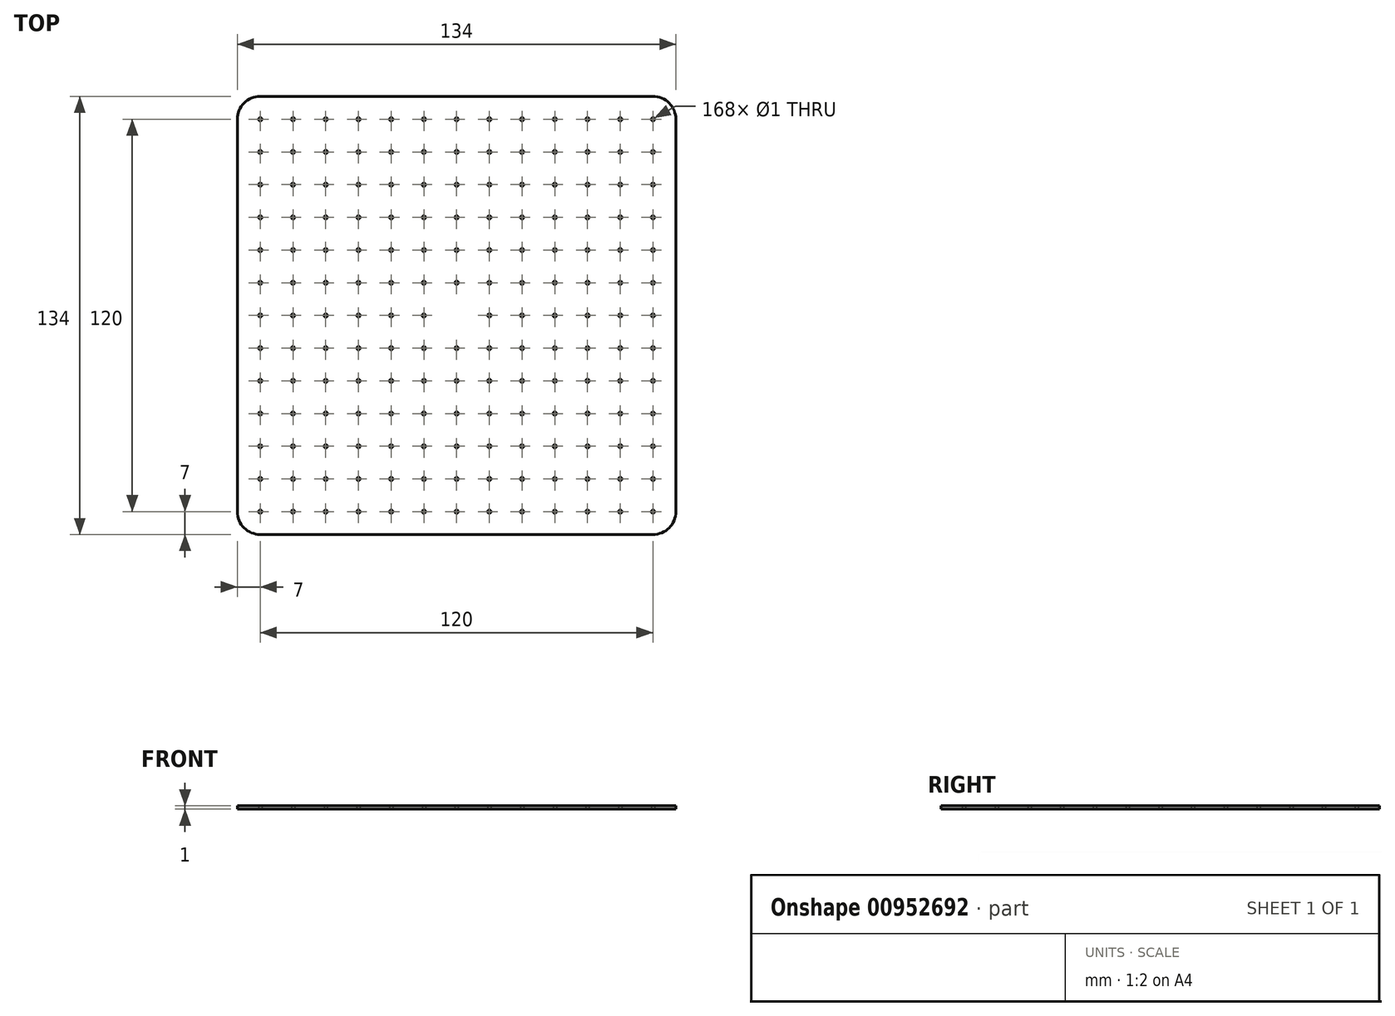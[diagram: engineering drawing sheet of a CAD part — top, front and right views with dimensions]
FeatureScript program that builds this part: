
annotation { "Feature Type Name" : "Feature", "Feature Type Description" : "" }
export const myFeature = defineFeature(function(context is Context, id is Id, definition is map)
    precondition{}
    {
        {
            var Q0;
            Q0=qCreatedBy(makeId("Top.planeOp"),FACE);
            var sketch = newSketch(context, id + "F0", { "sketchPlane" : qUnion([Q0])});
            skLineSegment(sketch, "E0.bottom", {"start": v(-60, -67) * mm, "end": v(60, -67) * mm});
            skLineSegment(sketch, "E0.top", {"start": v(-60, 67) * mm, "end": v(60, 67) * mm});
            skLineSegment(sketch, "E0.left", {"start": v(-67, -60) * mm, "end": v(-67, 60) * mm});
            skLineSegment(sketch, "E0.right", {"start": v(67, -60) * mm, "end": v(67, 60) * mm});
            skPoint(sketch, "E0.middle", {"position": v(0, 0) * mm});
            skPoint(sketch, "E1.visualSharp", {"position": v(-67, -67) * mm});
            skArc(sketch, "E1.filletArc", {"start": v(-67, -60) * mm, "mid": v(-64.95, -64.95) * mm, "end": v(-60, -67) * mm});
            skPoint(sketch, "E2.visualSharp", {"position": v(-67, 67) * mm});
            skArc(sketch, "E2.filletArc", {"start": v(-60, 67) * mm, "mid": v(-64.95, 64.95) * mm, "end": v(-67, 60) * mm});
            skPoint(sketch, "E3.visualSharp", {"position": v(67, 67) * mm});
            skArc(sketch, "E3.filletArc", {"start": v(67, 60) * mm, "mid": v(64.95, 64.95) * mm, "end": v(60, 67) * mm});
            skPoint(sketch, "E4.visualSharp", {"position": v(67, -67) * mm});
            skArc(sketch, "E4.filletArc", {"start": v(60, -67) * mm, "mid": v(64.95, -64.95) * mm, "end": v(67, -60) * mm});
            skCircle(sketch, "E5", {"center": v(-60, 60) * mm, "radius": 0.5 * mm});
            skCircle(sketch, "E6.0.1.0", {"center": v(-60, 50) * mm, "radius": 0.5 * mm});
            skCircle(sketch, "E6.0.2.0", {"center": v(-60, 40) * mm, "radius": 0.5 * mm});
            skCircle(sketch, "E6.0.3.0", {"center": v(-60, 30) * mm, "radius": 0.5 * mm});
            skCircle(sketch, "E6.0.4.0", {"center": v(-60, 20) * mm, "radius": 0.5 * mm});
            skCircle(sketch, "E6.0.5.0", {"center": v(-60, 10) * mm, "radius": 0.5 * mm});
            skCircle(sketch, "E6.0.6.0", {"center": v(-60, 0) * mm, "radius": 0.5 * mm});
            skCircle(sketch, "E6.0.7.0", {"center": v(-60, -10) * mm, "radius": 0.5 * mm});
            skCircle(sketch, "E6.0.8.0", {"center": v(-60, -20) * mm, "radius": 0.5 * mm});
            skCircle(sketch, "E6.0.9.0", {"center": v(-60, -30) * mm, "radius": 0.5 * mm});
            skCircle(sketch, "E6.0.10.0", {"center": v(-60, -40) * mm, "radius": 0.5 * mm});
            skCircle(sketch, "E6.0.11.0", {"center": v(-60, -50) * mm, "radius": 0.5 * mm});
            skCircle(sketch, "E6.1.0.0", {"center": v(-50, 60) * mm, "radius": 0.5 * mm});
            skCircle(sketch, "E6.1.1.0", {"center": v(-50, 50) * mm, "radius": 0.5 * mm});
            skCircle(sketch, "E6.1.2.0", {"center": v(-50, 40) * mm, "radius": 0.5 * mm});
            skCircle(sketch, "E6.1.3.0", {"center": v(-50, 30) * mm, "radius": 0.5 * mm});
            skCircle(sketch, "E6.1.4.0", {"center": v(-50, 20) * mm, "radius": 0.5 * mm});
            skCircle(sketch, "E6.1.5.0", {"center": v(-50, 10) * mm, "radius": 0.5 * mm});
            skCircle(sketch, "E6.1.6.0", {"center": v(-50, 0) * mm, "radius": 0.5 * mm});
            skCircle(sketch, "E6.1.7.0", {"center": v(-50, -10) * mm, "radius": 0.5 * mm});
            skCircle(sketch, "E6.1.8.0", {"center": v(-50, -20) * mm, "radius": 0.5 * mm});
            skCircle(sketch, "E6.1.9.0", {"center": v(-50, -30) * mm, "radius": 0.5 * mm});
            skCircle(sketch, "E6.1.10.0", {"center": v(-50, -40) * mm, "radius": 0.5 * mm});
            skCircle(sketch, "E6.1.11.0", {"center": v(-50, -50) * mm, "radius": 0.5 * mm});
            skCircle(sketch, "E6.2.0.0", {"center": v(-40, 60) * mm, "radius": 0.5 * mm});
            skCircle(sketch, "E6.2.1.0", {"center": v(-40, 50) * mm, "radius": 0.5 * mm});
            skCircle(sketch, "E6.2.2.0", {"center": v(-40, 40) * mm, "radius": 0.5 * mm});
            skCircle(sketch, "E6.2.3.0", {"center": v(-40, 30) * mm, "radius": 0.5 * mm});
            skCircle(sketch, "E6.2.4.0", {"center": v(-40, 20) * mm, "radius": 0.5 * mm});
            skCircle(sketch, "E6.2.5.0", {"center": v(-40, 10) * mm, "radius": 0.5 * mm});
            skCircle(sketch, "E6.2.6.0", {"center": v(-40, 0) * mm, "radius": 0.5 * mm});
            skCircle(sketch, "E6.2.7.0", {"center": v(-40, -10) * mm, "radius": 0.5 * mm});
            skCircle(sketch, "E6.2.8.0", {"center": v(-40, -20) * mm, "radius": 0.5 * mm});
            skCircle(sketch, "E6.2.9.0", {"center": v(-40, -30) * mm, "radius": 0.5 * mm});
            skCircle(sketch, "E6.2.10.0", {"center": v(-40, -40) * mm, "radius": 0.5 * mm});
            skCircle(sketch, "E6.2.11.0", {"center": v(-40, -50) * mm, "radius": 0.5 * mm});
            skCircle(sketch, "E6.3.0.0", {"center": v(-30, 60) * mm, "radius": 0.5 * mm});
            skCircle(sketch, "E6.3.1.0", {"center": v(-30, 50) * mm, "radius": 0.5 * mm});
            skCircle(sketch, "E6.3.2.0", {"center": v(-30, 40) * mm, "radius": 0.5 * mm});
            skCircle(sketch, "E6.3.3.0", {"center": v(-30, 30) * mm, "radius": 0.5 * mm});
            skCircle(sketch, "E6.3.4.0", {"center": v(-30, 20) * mm, "radius": 0.5 * mm});
            skCircle(sketch, "E6.3.5.0", {"center": v(-30, 10) * mm, "radius": 0.5 * mm});
            skCircle(sketch, "E6.3.6.0", {"center": v(-30, 0) * mm, "radius": 0.5 * mm});
            skCircle(sketch, "E6.3.7.0", {"center": v(-30, -10) * mm, "radius": 0.5 * mm});
            skCircle(sketch, "E6.3.8.0", {"center": v(-30, -20) * mm, "radius": 0.5 * mm});
            skCircle(sketch, "E6.3.9.0", {"center": v(-30, -30) * mm, "radius": 0.5 * mm});
            skCircle(sketch, "E6.3.10.0", {"center": v(-30, -40) * mm, "radius": 0.5 * mm});
            skCircle(sketch, "E6.3.11.0", {"center": v(-30, -50) * mm, "radius": 0.5 * mm});
            skCircle(sketch, "E6.4.0.0", {"center": v(-20, 60) * mm, "radius": 0.5 * mm});
            skCircle(sketch, "E6.4.1.0", {"center": v(-20, 50) * mm, "radius": 0.5 * mm});
            skCircle(sketch, "E6.4.2.0", {"center": v(-20, 40) * mm, "radius": 0.5 * mm});
            skCircle(sketch, "E6.4.3.0", {"center": v(-20, 30) * mm, "radius": 0.5 * mm});
            skCircle(sketch, "E6.4.4.0", {"center": v(-20, 20) * mm, "radius": 0.5 * mm});
            skCircle(sketch, "E6.4.5.0", {"center": v(-20, 10) * mm, "radius": 0.5 * mm});
            skCircle(sketch, "E6.4.6.0", {"center": v(-20, 0) * mm, "radius": 0.5 * mm});
            skCircle(sketch, "E6.4.7.0", {"center": v(-20, -10) * mm, "radius": 0.5 * mm});
            skCircle(sketch, "E6.4.8.0", {"center": v(-20, -20) * mm, "radius": 0.5 * mm});
            skCircle(sketch, "E6.4.9.0", {"center": v(-20, -30) * mm, "radius": 0.5 * mm});
            skCircle(sketch, "E6.4.10.0", {"center": v(-20, -40) * mm, "radius": 0.5 * mm});
            skCircle(sketch, "E6.4.11.0", {"center": v(-20, -50) * mm, "radius": 0.5 * mm});
            skCircle(sketch, "E6.5.0.0", {"center": v(-10, 60) * mm, "radius": 0.5 * mm});
            skCircle(sketch, "E6.5.1.0", {"center": v(-10, 50) * mm, "radius": 0.5 * mm});
            skCircle(sketch, "E6.5.2.0", {"center": v(-10, 40) * mm, "radius": 0.5 * mm});
            skCircle(sketch, "E6.5.3.0", {"center": v(-10, 30) * mm, "radius": 0.5 * mm});
            skCircle(sketch, "E6.5.4.0", {"center": v(-10, 20) * mm, "radius": 0.5 * mm});
            skCircle(sketch, "E6.5.5.0", {"center": v(-10, 10) * mm, "radius": 0.5 * mm});
            skCircle(sketch, "E6.5.6.0", {"center": v(-10, 0) * mm, "radius": 0.5 * mm});
            skCircle(sketch, "E6.5.7.0", {"center": v(-10, -10) * mm, "radius": 0.5 * mm});
            skCircle(sketch, "E6.5.8.0", {"center": v(-10, -20) * mm, "radius": 0.5 * mm});
            skCircle(sketch, "E6.5.9.0", {"center": v(-10, -30) * mm, "radius": 0.5 * mm});
            skCircle(sketch, "E6.5.10.0", {"center": v(-10, -40) * mm, "radius": 0.5 * mm});
            skCircle(sketch, "E6.5.11.0", {"center": v(-10, -50) * mm, "radius": 0.5 * mm});
            skCircle(sketch, "E6.6.0.0", {"center": v(0, 60) * mm, "radius": 0.5 * mm});
            skCircle(sketch, "E6.6.1.0", {"center": v(0, 50) * mm, "radius": 0.5 * mm});
            skCircle(sketch, "E6.6.2.0", {"center": v(0, 40) * mm, "radius": 0.5 * mm});
            skCircle(sketch, "E6.6.3.0", {"center": v(0, 30) * mm, "radius": 0.5 * mm});
            skCircle(sketch, "E6.6.4.0", {"center": v(0, 20) * mm, "radius": 0.5 * mm});
            skCircle(sketch, "E6.6.5.0", {"center": v(0, 10) * mm, "radius": 0.5 * mm});
            skCircle(sketch, "E6.6.6.0", {"center": v(0, 0) * mm, "radius": 0.5 * mm});
            skCircle(sketch, "E6.6.7.0", {"center": v(0, -10) * mm, "radius": 0.5 * mm});
            skCircle(sketch, "E6.6.8.0", {"center": v(0, -20) * mm, "radius": 0.5 * mm});
            skCircle(sketch, "E6.6.9.0", {"center": v(0, -30) * mm, "radius": 0.5 * mm});
            skCircle(sketch, "E6.6.10.0", {"center": v(0, -40) * mm, "radius": 0.5 * mm});
            skCircle(sketch, "E6.6.11.0", {"center": v(0, -50) * mm, "radius": 0.5 * mm});
            skCircle(sketch, "E6.7.0.0", {"center": v(10, 60) * mm, "radius": 0.5 * mm});
            skCircle(sketch, "E6.7.1.0", {"center": v(10, 50) * mm, "radius": 0.5 * mm});
            skCircle(sketch, "E6.7.2.0", {"center": v(10, 40) * mm, "radius": 0.5 * mm});
            skCircle(sketch, "E6.7.3.0", {"center": v(10, 30) * mm, "radius": 0.5 * mm});
            skCircle(sketch, "E6.7.4.0", {"center": v(10, 20) * mm, "radius": 0.5 * mm});
            skCircle(sketch, "E6.7.5.0", {"center": v(10, 10) * mm, "radius": 0.5 * mm});
            skCircle(sketch, "E6.7.6.0", {"center": v(10, 0) * mm, "radius": 0.5 * mm});
            skCircle(sketch, "E6.7.7.0", {"center": v(10, -10) * mm, "radius": 0.5 * mm});
            skCircle(sketch, "E6.7.8.0", {"center": v(10, -20) * mm, "radius": 0.5 * mm});
            skCircle(sketch, "E6.7.9.0", {"center": v(10, -30) * mm, "radius": 0.5 * mm});
            skCircle(sketch, "E6.7.10.0", {"center": v(10, -40) * mm, "radius": 0.5 * mm});
            skCircle(sketch, "E6.7.11.0", {"center": v(10, -50) * mm, "radius": 0.5 * mm});
            skCircle(sketch, "E6.8.0.0", {"center": v(20, 60) * mm, "radius": 0.5 * mm});
            skCircle(sketch, "E6.8.1.0", {"center": v(20, 50) * mm, "radius": 0.5 * mm});
            skCircle(sketch, "E6.8.2.0", {"center": v(20, 40) * mm, "radius": 0.5 * mm});
            skCircle(sketch, "E6.8.3.0", {"center": v(20, 30) * mm, "radius": 0.5 * mm});
            skCircle(sketch, "E6.8.4.0", {"center": v(20, 20) * mm, "radius": 0.5 * mm});
            skCircle(sketch, "E6.8.5.0", {"center": v(20, 10) * mm, "radius": 0.5 * mm});
            skCircle(sketch, "E6.8.6.0", {"center": v(20, 0) * mm, "radius": 0.5 * mm});
            skCircle(sketch, "E6.8.7.0", {"center": v(20, -10) * mm, "radius": 0.5 * mm});
            skCircle(sketch, "E6.8.8.0", {"center": v(20, -20) * mm, "radius": 0.5 * mm});
            skCircle(sketch, "E6.8.9.0", {"center": v(20, -30) * mm, "radius": 0.5 * mm});
            skCircle(sketch, "E6.8.10.0", {"center": v(20, -40) * mm, "radius": 0.5 * mm});
            skCircle(sketch, "E6.8.11.0", {"center": v(20, -50) * mm, "radius": 0.5 * mm});
            skCircle(sketch, "E6.9.0.0", {"center": v(30, 60) * mm, "radius": 0.5 * mm});
            skCircle(sketch, "E6.9.1.0", {"center": v(30, 50) * mm, "radius": 0.5 * mm});
            skCircle(sketch, "E6.9.2.0", {"center": v(30, 40) * mm, "radius": 0.5 * mm});
            skCircle(sketch, "E6.9.3.0", {"center": v(30, 30) * mm, "radius": 0.5 * mm});
            skCircle(sketch, "E6.9.4.0", {"center": v(30, 20) * mm, "radius": 0.5 * mm});
            skCircle(sketch, "E6.9.5.0", {"center": v(30, 10) * mm, "radius": 0.5 * mm});
            skCircle(sketch, "E6.9.6.0", {"center": v(30, 0) * mm, "radius": 0.5 * mm});
            skCircle(sketch, "E6.9.7.0", {"center": v(30, -10) * mm, "radius": 0.5 * mm});
            skCircle(sketch, "E6.9.8.0", {"center": v(30, -20) * mm, "radius": 0.5 * mm});
            skCircle(sketch, "E6.9.9.0", {"center": v(30, -30) * mm, "radius": 0.5 * mm});
            skCircle(sketch, "E6.9.10.0", {"center": v(30, -40) * mm, "radius": 0.5 * mm});
            skCircle(sketch, "E6.9.11.0", {"center": v(30, -50) * mm, "radius": 0.5 * mm});
            skCircle(sketch, "E6.10.0.0", {"center": v(40, 60) * mm, "radius": 0.5 * mm});
            skCircle(sketch, "E6.10.1.0", {"center": v(40, 50) * mm, "radius": 0.5 * mm});
            skCircle(sketch, "E6.10.2.0", {"center": v(40, 40) * mm, "radius": 0.5 * mm});
            skCircle(sketch, "E6.10.3.0", {"center": v(40, 30) * mm, "radius": 0.5 * mm});
            skCircle(sketch, "E6.10.4.0", {"center": v(40, 20) * mm, "radius": 0.5 * mm});
            skCircle(sketch, "E6.10.5.0", {"center": v(40, 10) * mm, "radius": 0.5 * mm});
            skCircle(sketch, "E6.10.6.0", {"center": v(40, 0) * mm, "radius": 0.5 * mm});
            skCircle(sketch, "E6.10.7.0", {"center": v(40, -10) * mm, "radius": 0.5 * mm});
            skCircle(sketch, "E6.10.8.0", {"center": v(40, -20) * mm, "radius": 0.5 * mm});
            skCircle(sketch, "E6.10.9.0", {"center": v(40, -30) * mm, "radius": 0.5 * mm});
            skCircle(sketch, "E6.10.10.0", {"center": v(40, -40) * mm, "radius": 0.5 * mm});
            skCircle(sketch, "E6.10.11.0", {"center": v(40, -50) * mm, "radius": 0.5 * mm});
            skCircle(sketch, "E6.11.0.0", {"center": v(50, 60) * mm, "radius": 0.5 * mm});
            skCircle(sketch, "E6.11.1.0", {"center": v(50, 50) * mm, "radius": 0.5 * mm});
            skCircle(sketch, "E6.11.2.0", {"center": v(50, 40) * mm, "radius": 0.5 * mm});
            skCircle(sketch, "E6.11.3.0", {"center": v(50, 30) * mm, "radius": 0.5 * mm});
            skCircle(sketch, "E6.11.4.0", {"center": v(50, 20) * mm, "radius": 0.5 * mm});
            skCircle(sketch, "E6.11.5.0", {"center": v(50, 10) * mm, "radius": 0.5 * mm});
            skCircle(sketch, "E6.11.6.0", {"center": v(50, 0) * mm, "radius": 0.5 * mm});
            skCircle(sketch, "E6.11.7.0", {"center": v(50, -10) * mm, "radius": 0.5 * mm});
            skCircle(sketch, "E6.11.8.0", {"center": v(50, -20) * mm, "radius": 0.5 * mm});
            skCircle(sketch, "E6.11.9.0", {"center": v(50, -30) * mm, "radius": 0.5 * mm});
            skCircle(sketch, "E6.11.10.0", {"center": v(50, -40) * mm, "radius": 0.5 * mm});
            skCircle(sketch, "E6.11.11.0", {"center": v(50, -50) * mm, "radius": 0.5 * mm});
            skCircle(sketch, "E6.12.0.0", {"center": v(60, 60) * mm, "radius": 0.5 * mm});
            skCircle(sketch, "E6.12.1.0", {"center": v(60, 50) * mm, "radius": 0.5 * mm});
            skCircle(sketch, "E6.12.2.0", {"center": v(60, 40) * mm, "radius": 0.5 * mm});
            skCircle(sketch, "E6.12.3.0", {"center": v(60, 30) * mm, "radius": 0.5 * mm});
            skCircle(sketch, "E6.12.4.0", {"center": v(60, 20) * mm, "radius": 0.5 * mm});
            skCircle(sketch, "E6.12.5.0", {"center": v(60, 10) * mm, "radius": 0.5 * mm});
            skCircle(sketch, "E6.12.6.0", {"center": v(60, 0) * mm, "radius": 0.5 * mm});
            skCircle(sketch, "E6.12.7.0", {"center": v(60, -10) * mm, "radius": 0.5 * mm});
            skCircle(sketch, "E6.12.8.0", {"center": v(60, -20) * mm, "radius": 0.5 * mm});
            skCircle(sketch, "E6.12.9.0", {"center": v(60, -30) * mm, "radius": 0.5 * mm});
            skCircle(sketch, "E6.12.10.0", {"center": v(60, -40) * mm, "radius": 0.5 * mm});
            skCircle(sketch, "E6.12.11.0", {"center": v(60, -50) * mm, "radius": 0.5 * mm});
            skLineSegment(sketch, "E6.direction1", {"start": v(-57, 57) * mm, "end": v(-47, 57) * mm, "construction": true});
            skLineSegment(sketch, "E6.direction2", {"start": v(-57, 57) * mm, "end": v(-57, 47) * mm, "construction": true});
            skCircle(sketch, "E7.0.0.12", {"center": v(-60, -60) * mm, "radius": 0.5 * mm});
            skCircle(sketch, "E7.0.1.12", {"center": v(-50, -60) * mm, "radius": 0.5 * mm});
            skCircle(sketch, "E7.0.2.12", {"center": v(-40, -60) * mm, "radius": 0.5 * mm});
            skCircle(sketch, "E7.0.3.12", {"center": v(-30, -60) * mm, "radius": 0.5 * mm});
            skCircle(sketch, "E7.0.4.12", {"center": v(-20, -60) * mm, "radius": 0.5 * mm});
            skCircle(sketch, "E7.0.5.12", {"center": v(-10, -60) * mm, "radius": 0.5 * mm});
            skCircle(sketch, "E7.0.6.12", {"center": v(0, -60) * mm, "radius": 0.5 * mm});
            skCircle(sketch, "E7.0.7.12", {"center": v(10, -60) * mm, "radius": 0.5 * mm});
            skCircle(sketch, "E7.0.8.12", {"center": v(20, -60) * mm, "radius": 0.5 * mm});
            skCircle(sketch, "E7.0.9.12", {"center": v(30, -60) * mm, "radius": 0.5 * mm});
            skCircle(sketch, "E7.0.10.12", {"center": v(40, -60) * mm, "radius": 0.5 * mm});
            skCircle(sketch, "E7.0.11.12", {"center": v(50, -60) * mm, "radius": 0.5 * mm});
            skCircle(sketch, "E7.0.12.12", {"center": v(60, -60) * mm, "radius": 0.5 * mm});
            skSolve(sketch);
        }
        {
            var Q0;
            Q0=makeQuery(id+"F0.imprint","IMPRINT",FACE,{"disambiguationData":[TD([[makeQuery(id+"F0.imprint","IMPRINT",EDGE,{"derivedFrom":sQuery(id+"F0.wireOp",EDGE,"E0.bottom")}),1.0]])]});
            extrude(context, id + "F1", {"entities" : qUnion([Q0]), "depth" : 1 * mm, "offsetDistance" : 25 * mm});
        }
        {
            var Q0;
            Q0=makeQuery(id+"F1.opExtrude","CAP_FACE",FACE,{"disambiguationData":[OSD([sQuery(id+"F0.wireOp",EDGE,"E0.bottom"),sQuery(id+"F0.wireOp",EDGE,"E0.top"),sQuery(id+"F0.wireOp",EDGE,"E0.left"),sQuery(id+"F0.wireOp",EDGE,"E0.right"),sQuery(id+"F0.wireOp",EDGE,"E1.filletArc"),sQuery(id+"F0.wireOp",EDGE,"E2.filletArc"),sQuery(id+"F0.wireOp",EDGE,"E3.filletArc"),sQuery(id+"F0.wireOp",EDGE,"E4.filletArc"),sQuery(id+"F0.wireOp",EDGE,"E5"),sQuery(id+"F0.wireOp",EDGE,"E6.0.1.0"),sQuery(id+"F0.wireOp",EDGE,"E6.0.2.0"),sQuery(id+"F0.wireOp",EDGE,"E6.0.3.0"),sQuery(id+"F0.wireOp",EDGE,"E6.0.4.0"),sQuery(id+"F0.wireOp",EDGE,"E6.0.5.0"),sQuery(id+"F0.wireOp",EDGE,"E6.0.6.0"),sQuery(id+"F0.wireOp",EDGE,"E6.0.7.0"),sQuery(id+"F0.wireOp",EDGE,"E6.0.8.0"),sQuery(id+"F0.wireOp",EDGE,"E6.0.9.0"),sQuery(id+"F0.wireOp",EDGE,"E6.0.10.0"),sQuery(id+"F0.wireOp",EDGE,"E6.0.11.0"),sQuery(id+"F0.wireOp",EDGE,"E6.1.0.0"),sQuery(id+"F0.wireOp",EDGE,"E6.1.1.0"),sQuery(id+"F0.wireOp",EDGE,"E6.1.2.0"),sQuery(id+"F0.wireOp",EDGE,"E6.1.3.0"),sQuery(id+"F0.wireOp",EDGE,"E6.1.4.0"),sQuery(id+"F0.wireOp",EDGE,"E6.1.5.0"),sQuery(id+"F0.wireOp",EDGE,"E6.1.6.0"),sQuery(id+"F0.wireOp",EDGE,"E6.1.7.0"),sQuery(id+"F0.wireOp",EDGE,"E6.1.8.0"),sQuery(id+"F0.wireOp",EDGE,"E6.1.9.0"),sQuery(id+"F0.wireOp",EDGE,"E6.1.10.0"),sQuery(id+"F0.wireOp",EDGE,"E6.1.11.0"),sQuery(id+"F0.wireOp",EDGE,"E6.2.0.0"),sQuery(id+"F0.wireOp",EDGE,"E6.2.1.0"),sQuery(id+"F0.wireOp",EDGE,"E6.2.2.0"),sQuery(id+"F0.wireOp",EDGE,"E6.2.3.0"),sQuery(id+"F0.wireOp",EDGE,"E6.2.4.0"),sQuery(id+"F0.wireOp",EDGE,"E6.2.5.0"),sQuery(id+"F0.wireOp",EDGE,"E6.2.6.0"),sQuery(id+"F0.wireOp",EDGE,"E6.2.7.0"),sQuery(id+"F0.wireOp",EDGE,"E6.2.8.0"),sQuery(id+"F0.wireOp",EDGE,"E6.2.9.0"),sQuery(id+"F0.wireOp",EDGE,"E6.2.10.0"),sQuery(id+"F0.wireOp",EDGE,"E6.2.11.0"),sQuery(id+"F0.wireOp",EDGE,"E6.3.0.0"),sQuery(id+"F0.wireOp",EDGE,"E6.3.1.0"),sQuery(id+"F0.wireOp",EDGE,"E6.3.2.0"),sQuery(id+"F0.wireOp",EDGE,"E6.3.3.0"),sQuery(id+"F0.wireOp",EDGE,"E6.3.4.0"),sQuery(id+"F0.wireOp",EDGE,"E6.3.5.0"),sQuery(id+"F0.wireOp",EDGE,"E6.3.6.0"),sQuery(id+"F0.wireOp",EDGE,"E6.3.7.0"),sQuery(id+"F0.wireOp",EDGE,"E6.3.8.0"),sQuery(id+"F0.wireOp",EDGE,"E6.3.9.0"),sQuery(id+"F0.wireOp",EDGE,"E6.3.10.0"),sQuery(id+"F0.wireOp",EDGE,"E6.3.11.0"),sQuery(id+"F0.wireOp",EDGE,"E6.4.0.0"),sQuery(id+"F0.wireOp",EDGE,"E6.4.1.0"),sQuery(id+"F0.wireOp",EDGE,"E6.4.2.0"),sQuery(id+"F0.wireOp",EDGE,"E6.4.3.0"),sQuery(id+"F0.wireOp",EDGE,"E6.4.4.0"),sQuery(id+"F0.wireOp",EDGE,"E6.4.5.0"),sQuery(id+"F0.wireOp",EDGE,"E6.4.6.0"),sQuery(id+"F0.wireOp",EDGE,"E6.4.7.0"),sQuery(id+"F0.wireOp",EDGE,"E6.4.8.0"),sQuery(id+"F0.wireOp",EDGE,"E6.4.9.0"),sQuery(id+"F0.wireOp",EDGE,"E6.4.10.0"),sQuery(id+"F0.wireOp",EDGE,"E6.4.11.0"),sQuery(id+"F0.wireOp",EDGE,"E6.5.0.0"),sQuery(id+"F0.wireOp",EDGE,"E6.5.1.0"),sQuery(id+"F0.wireOp",EDGE,"E6.5.2.0"),sQuery(id+"F0.wireOp",EDGE,"E6.5.3.0"),sQuery(id+"F0.wireOp",EDGE,"E6.5.4.0"),sQuery(id+"F0.wireOp",EDGE,"E6.5.5.0"),sQuery(id+"F0.wireOp",EDGE,"E6.5.6.0"),sQuery(id+"F0.wireOp",EDGE,"E6.5.7.0"),sQuery(id+"F0.wireOp",EDGE,"E6.5.8.0"),sQuery(id+"F0.wireOp",EDGE,"E6.5.9.0"),sQuery(id+"F0.wireOp",EDGE,"E6.5.10.0"),sQuery(id+"F0.wireOp",EDGE,"E6.5.11.0"),sQuery(id+"F0.wireOp",EDGE,"E6.6.0.0"),sQuery(id+"F0.wireOp",EDGE,"E6.6.1.0"),sQuery(id+"F0.wireOp",EDGE,"E6.6.2.0"),sQuery(id+"F0.wireOp",EDGE,"E6.6.3.0"),sQuery(id+"F0.wireOp",EDGE,"E6.6.4.0"),sQuery(id+"F0.wireOp",EDGE,"E6.6.5.0"),sQuery(id+"F0.wireOp",EDGE,"E6.6.6.0"),sQuery(id+"F0.wireOp",EDGE,"E6.6.7.0"),sQuery(id+"F0.wireOp",EDGE,"E6.6.8.0"),sQuery(id+"F0.wireOp",EDGE,"E6.6.9.0"),sQuery(id+"F0.wireOp",EDGE,"E6.6.10.0"),sQuery(id+"F0.wireOp",EDGE,"E6.6.11.0"),sQuery(id+"F0.wireOp",EDGE,"E6.7.0.0"),sQuery(id+"F0.wireOp",EDGE,"E6.7.1.0"),sQuery(id+"F0.wireOp",EDGE,"E6.7.2.0"),sQuery(id+"F0.wireOp",EDGE,"E6.7.3.0"),sQuery(id+"F0.wireOp",EDGE,"E6.7.4.0"),sQuery(id+"F0.wireOp",EDGE,"E6.7.5.0"),sQuery(id+"F0.wireOp",EDGE,"E6.7.6.0"),sQuery(id+"F0.wireOp",EDGE,"E6.7.7.0"),sQuery(id+"F0.wireOp",EDGE,"E6.7.8.0"),sQuery(id+"F0.wireOp",EDGE,"E6.7.9.0"),sQuery(id+"F0.wireOp",EDGE,"E6.7.10.0"),sQuery(id+"F0.wireOp",EDGE,"E6.7.11.0"),sQuery(id+"F0.wireOp",EDGE,"E6.8.0.0"),sQuery(id+"F0.wireOp",EDGE,"E6.8.1.0"),sQuery(id+"F0.wireOp",EDGE,"E6.8.2.0"),sQuery(id+"F0.wireOp",EDGE,"E6.8.3.0"),sQuery(id+"F0.wireOp",EDGE,"E6.8.4.0"),sQuery(id+"F0.wireOp",EDGE,"E6.8.5.0"),sQuery(id+"F0.wireOp",EDGE,"E6.8.6.0"),sQuery(id+"F0.wireOp",EDGE,"E6.8.7.0"),sQuery(id+"F0.wireOp",EDGE,"E6.8.8.0"),sQuery(id+"F0.wireOp",EDGE,"E6.8.9.0"),sQuery(id+"F0.wireOp",EDGE,"E6.8.10.0"),sQuery(id+"F0.wireOp",EDGE,"E6.8.11.0"),sQuery(id+"F0.wireOp",EDGE,"E6.9.0.0"),sQuery(id+"F0.wireOp",EDGE,"E6.9.1.0"),sQuery(id+"F0.wireOp",EDGE,"E6.9.2.0"),sQuery(id+"F0.wireOp",EDGE,"E6.9.3.0"),sQuery(id+"F0.wireOp",EDGE,"E6.9.4.0"),sQuery(id+"F0.wireOp",EDGE,"E6.9.5.0"),sQuery(id+"F0.wireOp",EDGE,"E6.9.6.0"),sQuery(id+"F0.wireOp",EDGE,"E6.9.7.0"),sQuery(id+"F0.wireOp",EDGE,"E6.9.8.0"),sQuery(id+"F0.wireOp",EDGE,"E6.9.9.0"),sQuery(id+"F0.wireOp",EDGE,"E6.9.10.0"),sQuery(id+"F0.wireOp",EDGE,"E6.9.11.0"),sQuery(id+"F0.wireOp",EDGE,"E6.10.0.0"),sQuery(id+"F0.wireOp",EDGE,"E6.10.1.0"),sQuery(id+"F0.wireOp",EDGE,"E6.10.2.0"),sQuery(id+"F0.wireOp",EDGE,"E6.10.3.0"),sQuery(id+"F0.wireOp",EDGE,"E6.10.4.0"),sQuery(id+"F0.wireOp",EDGE,"E6.10.5.0"),sQuery(id+"F0.wireOp",EDGE,"E6.10.6.0"),sQuery(id+"F0.wireOp",EDGE,"E6.10.7.0"),sQuery(id+"F0.wireOp",EDGE,"E6.10.8.0"),sQuery(id+"F0.wireOp",EDGE,"E6.10.9.0"),sQuery(id+"F0.wireOp",EDGE,"E6.10.10.0"),sQuery(id+"F0.wireOp",EDGE,"E6.10.11.0"),sQuery(id+"F0.wireOp",EDGE,"E6.11.0.0"),sQuery(id+"F0.wireOp",EDGE,"E6.11.1.0"),sQuery(id+"F0.wireOp",EDGE,"E6.11.2.0"),sQuery(id+"F0.wireOp",EDGE,"E6.11.3.0"),sQuery(id+"F0.wireOp",EDGE,"E6.11.4.0"),sQuery(id+"F0.wireOp",EDGE,"E6.11.5.0"),sQuery(id+"F0.wireOp",EDGE,"E6.11.6.0"),sQuery(id+"F0.wireOp",EDGE,"E6.11.7.0"),sQuery(id+"F0.wireOp",EDGE,"E6.11.8.0"),sQuery(id+"F0.wireOp",EDGE,"E6.11.9.0"),sQuery(id+"F0.wireOp",EDGE,"E6.11.10.0"),sQuery(id+"F0.wireOp",EDGE,"E6.11.11.0"),sQuery(id+"F0.wireOp",EDGE,"E6.12.0.0"),sQuery(id+"F0.wireOp",EDGE,"E6.12.1.0"),sQuery(id+"F0.wireOp",EDGE,"E6.12.2.0"),sQuery(id+"F0.wireOp",EDGE,"E6.12.3.0"),sQuery(id+"F0.wireOp",EDGE,"E6.12.4.0"),sQuery(id+"F0.wireOp",EDGE,"E6.12.5.0"),sQuery(id+"F0.wireOp",EDGE,"E6.12.6.0"),sQuery(id+"F0.wireOp",EDGE,"E6.12.7.0"),sQuery(id+"F0.wireOp",EDGE,"E6.12.8.0"),sQuery(id+"F0.wireOp",EDGE,"E6.12.9.0"),sQuery(id+"F0.wireOp",EDGE,"E6.12.10.0"),sQuery(id+"F0.wireOp",EDGE,"E6.12.11.0"),sQuery(id+"F0.wireOp",EDGE,"E7.0.0.12"),sQuery(id+"F0.wireOp",EDGE,"E7.0.1.12"),sQuery(id+"F0.wireOp",EDGE,"E7.0.2.12"),sQuery(id+"F0.wireOp",EDGE,"E7.0.3.12"),sQuery(id+"F0.wireOp",EDGE,"E7.0.4.12"),sQuery(id+"F0.wireOp",EDGE,"E7.0.5.12"),sQuery(id+"F0.wireOp",EDGE,"E7.0.6.12"),sQuery(id+"F0.wireOp",EDGE,"E7.0.7.12"),sQuery(id+"F0.wireOp",EDGE,"E7.0.8.12"),sQuery(id+"F0.wireOp",EDGE,"E7.0.9.12"),sQuery(id+"F0.wireOp",EDGE,"E7.0.10.12"),sQuery(id+"F0.wireOp",EDGE,"E7.0.11.12"),sQuery(id+"F0.wireOp",EDGE,"E7.0.12.12")])],"isStart":false});
            var sketch = newSketch(context, id + "F2", { "sketchPlane" : qUnion([Q0])});
            skCircle(sketch, "E8", {"center": v(0, 0) * mm, "radius": 1.08 * mm});
            skSolve(sketch);
        }
        {
            var Q0;
            Q0 = qSketchRegion(id + "F2", true);
            extrude(context, id + "F3", {"entities" : qUnion([Q0]), "operationType" : NewBodyOperationType.ADD, "oppositeDirection" : true, "depth" : 1 * mm, "offsetDistance" : 25 * mm});
        }
    });
